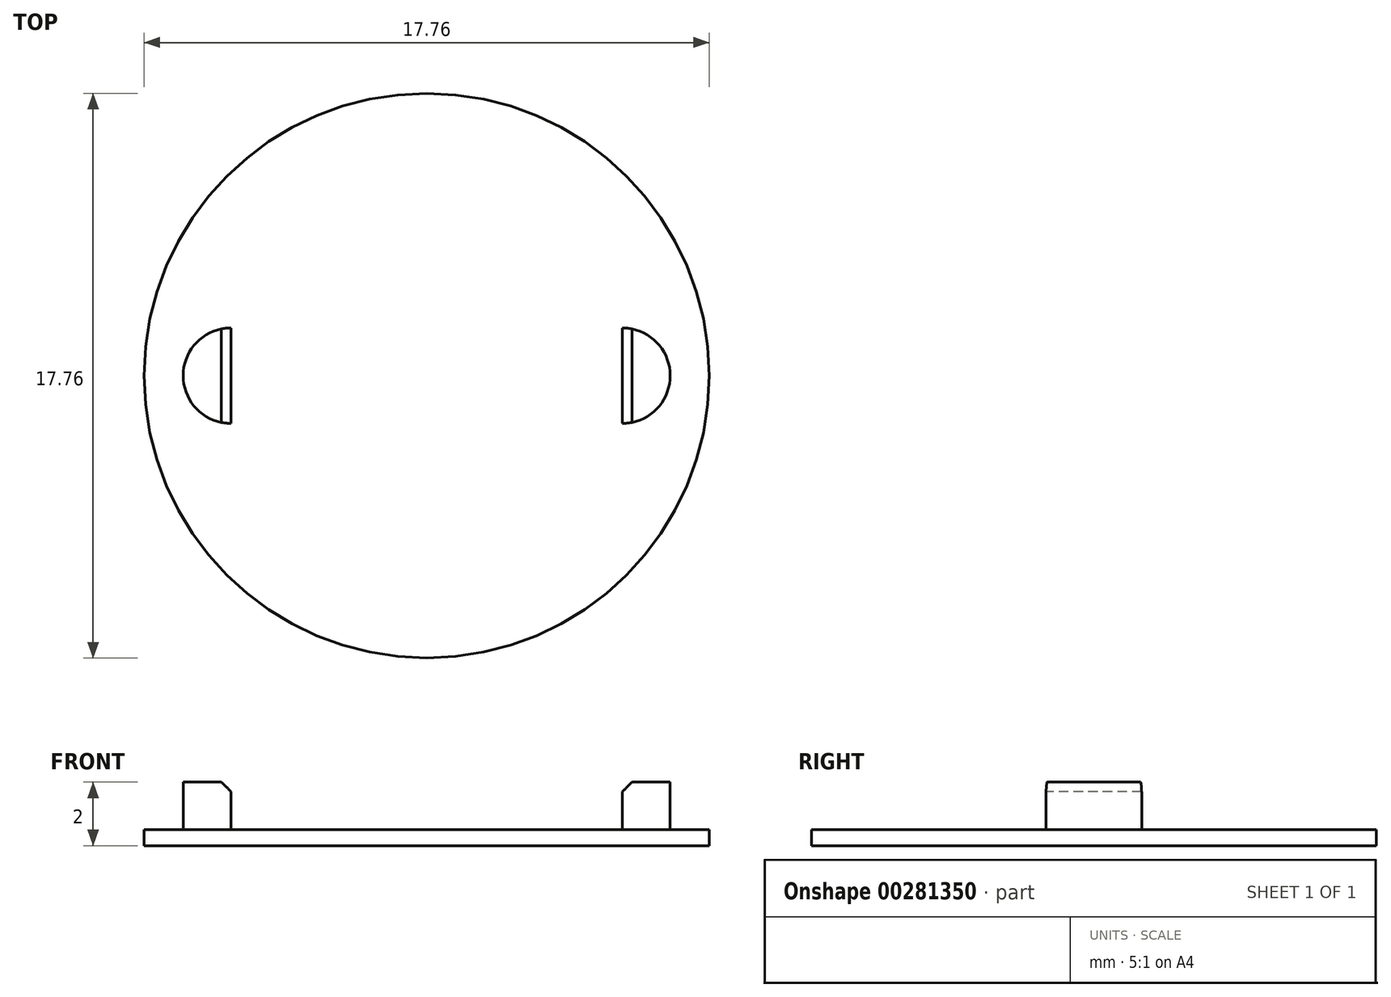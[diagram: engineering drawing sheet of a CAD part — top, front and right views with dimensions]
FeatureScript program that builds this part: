
annotation { "Feature Type Name" : "Feature", "Feature Type Description" : "" }
export const myFeature = defineFeature(function(context is Context, id is Id, definition is map)
    precondition{}
    {
        {
            var Q0;
            Q0=qCreatedBy(makeId("Top.planeOp"),FACE);
            var sketch = newSketch(context, id + "F0", { "sketchPlane" : qUnion([Q0])});
            skCircle(sketch, "E0", {"center": v(0, 0) * mm, "radius": 8.88 * mm});
            skSolve(sketch);
        }
        {
            var Q0;
            Q0 = qSketchRegion(id + "F0", true);
            extrude(context, id + "F1", {"entities" : qUnion([Q0]), "depth" : 0.5 * mm});
        }
        {
            var Q0;
            Q0=makeQuery(id+"F1.opExtrude","CAP_FACE",FACE,{"disambiguationData":[OSD([sQuery(id+"F0.wireOp",EDGE,"E0")])],"isStart":false});
            var sketch = newSketch(context, id + "F2", { "sketchPlane" : qUnion([Q0])});
            skArc(sketch, "E1", {"start": v(-6.15, 1.5) * mm, "mid": v(-7.65, 0) * mm, "end": v(-6.15, -1.5) * mm});
            skLineSegment(sketch, "E2", {"start": v(-6.15, 1.5) * mm, "end": v(-6.15, -1.5) * mm});
            skLineSegment(sketch, "E3.MirrorCS", {"start": v(6.15, 1.5) * mm, "end": v(6.15, -1.5) * mm});
            skArc(sketch, "E4.MirrorCS", {"start": v(6.15, 1.5) * mm, "mid": v(7.65, 0) * mm, "end": v(6.15, -1.5) * mm});
            skSolve(sketch);
        }
        {
            var Q0;
            Q0=makeQuery(id+"F2.imprint","IMPRINT",FACE,{"disambiguationData":[TD([[makeQuery(id+"F2.imprint","IMPRINT",EDGE,{"derivedFrom":sQuery(id+"F2.wireOp",EDGE,"E1")}),1.0]])]});
            var Q1;
            Q1=makeQuery(id+"F2.imprint","IMPRINT",FACE,{"disambiguationData":[TD([[makeQuery(id+"F2.imprint","IMPRINT",EDGE,{"derivedFrom":sQuery(id+"F2.wireOp",EDGE,"E3.MirrorCS")}),1.0]])]});
            extrude(context, id + "F3", {"entities" : qUnion([Q0, Q1]), "operationType" : NewBodyOperationType.ADD, "depth" : 1.5 * mm});
        }
        {
            var Q0;
            Q0=makeQuery(id+"F3.opExtrude","CAP_EDGE",EDGE,{"disambiguationData":[OSD([sQuery(id+"F2.wireOp",EDGE,"E2")])],"isStart":false});
            var Q1;
            Q1=makeQuery(id+"F3.opExtrude","CAP_EDGE",EDGE,{"disambiguationData":[OSD([sQuery(id+"F2.wireOp",EDGE,"E3.MirrorCS")])],"isStart":false});
            chamfer(context, id + "F4", {"entities" : qUnion([Q0, Q1]), "width" : 0.3 * mm, "tangentPropagation" : true});
        }
    });
